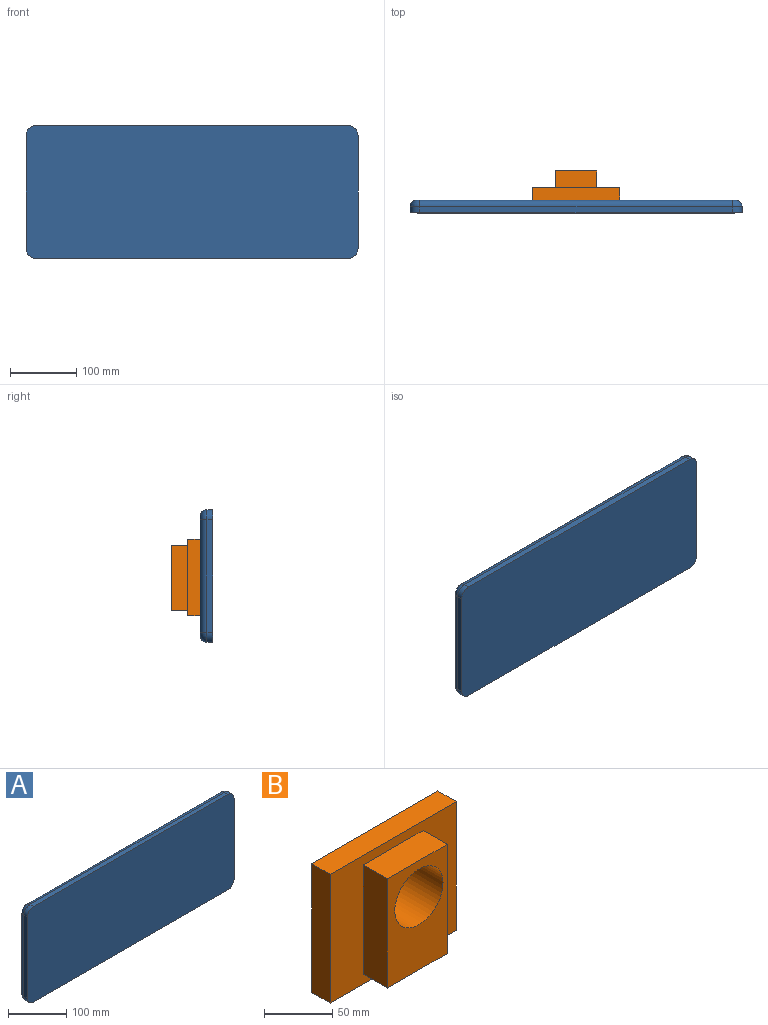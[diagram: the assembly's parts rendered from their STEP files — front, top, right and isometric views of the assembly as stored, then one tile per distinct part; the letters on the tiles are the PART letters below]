
ASSEMBLY  parts=2 mates=1
PART A: 18 faces, bbox 500x19x200 mm
  f0: plane 470x9mm, normal (0,0,1), area 4230mm2, adj f5,f6,f9,f16
  f1: plane 170x9mm, normal (-1,0,0), area 1530mm2, adj f5,f6,f7,f15
  f2: plane 470x9mm, normal (0,0,-1), area 4230mm2, adj f5,f7,f8,f11
  f3: plane 170x9mm, normal (1,0,0), area 1530mm2, adj f5,f8,f9,f12
  f4: plane 480x180mm, normal (0,1,0), area 86378.5mm2, adj f10,f11,f12,f13,f14,f15,f16,f17
  f5: plane 500x200mm, normal (0,-1,0), area 99806.9mm2, adj f0,f1,f2,f3,f6,f7,f8,f9
  f6: cylinder r=15mm len=15mm, axis (0,1,0), area 212.1mm2, adj f0,f1,f5,f17
  f7: cylinder r=15mm len=15mm, axis (0,-1,0), area 212.1mm2, adj f1,f2,f5,f13
  f8: cylinder r=15mm len=15mm, axis (0,1,0), area 212.1mm2, adj f2,f3,f5,f10
  f9: cylinder r=15mm len=15mm, axis (0,-1,0), area 212.1mm2, adj f0,f3,f5,f14
  f10: torus R=5mm, axis (0,-1,0), area 280.4mm2, adj f4,f8,f11,f12
  f11: cylinder r=10mm len=470mm, axis (-1,0,0), area 7382.7mm2, adj f2,f4,f10,f13
  f12: cylinder r=10mm len=170mm, axis (0,0,-1), area 2670.4mm2, adj f3,f4,f10,f14
  f13: torus R=5mm, axis (0,-1,0), area 280.4mm2, adj f4,f7,f11,f15
  f14: torus R=5mm, axis (0,-1,0), area 280.4mm2, adj f4,f9,f12,f16
  f15: cylinder r=10mm len=170mm, axis (0,0,1), area 2670.4mm2, adj f1,f4,f13,f17
  f16: cylinder r=10mm len=470mm, axis (1,0,0), area 7382.7mm2, adj f0,f4,f14,f17
  f17: torus R=5mm, axis (0,-1,0), area 280.4mm2, adj f4,f6,f15,f16
PART B: 12 faces, bbox 130.7x44x115.5 mm
  f0: plane 130.71x115.52mm, normal (0,-1,0), area 9020.6mm2, adj f1,f2,f3,f4,f6,f7,f8,f9
  f1: plane 130.71x19mm, normal (0,0,1), area 2483.4mm2, adj f0,f2,f4,f5
  f2: plane 115.52x19mm, normal (-1,0,0), area 2194.9mm2, adj f0,f1,f3,f5
  f3: plane 130.71x19mm, normal (0,0,-1), area 2483.4mm2, adj f0,f2,f4,f5
  f4: plane 115.52x19mm, normal (1,0,0), area 2194.9mm2, adj f0,f1,f3,f5
  f5: plane 130.71x115.52mm, normal (0,1,0), area 13135.7mm2, adj f1,f2,f3,f4,f11
  f6: plane 62.01x25mm, normal (0,0,1), area 1550.1mm2, adj f0,f7,f9,f10
  f7: plane 98.03x25mm, normal (-1,0,0), area 2450.8mm2, adj f0,f6,f8,f10
  f8: plane 62.01x25mm, normal (0,0,-1), area 1550.1mm2, adj f0,f7,f9,f10
  f9: plane 98.03x25mm, normal (1,0,0), area 2450.8mm2, adj f0,f6,f8,f10
  f10: plane 98.03x62.01mm, normal (0,-1,0), area 4115mm2, adj f6,f7,f8,f9,f11
  f11: cylinder r=25mm len=50mm, axis (0,-1,0), area 6911.5mm2, adj f5,f10
PLACE A t=(78.7,-50.46,-37.3)mm fixed
PLACE B rot(axis=(1,0,0),180deg) t=(81.2,-31.46,-119.97)mm
MATE planar B.f5 <-> A.f4  axis (0,-1,0) through (80.95,-31.46,-117.49)mm
